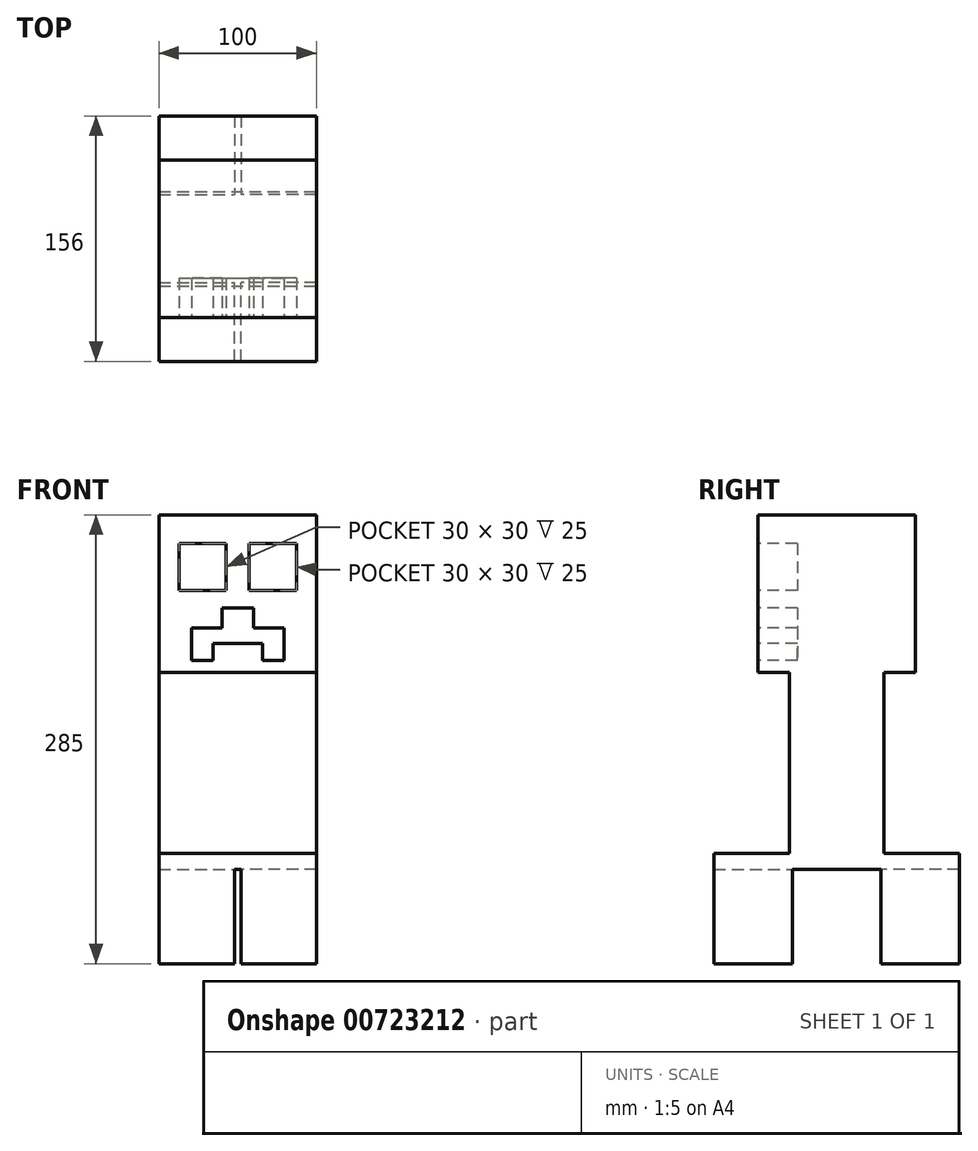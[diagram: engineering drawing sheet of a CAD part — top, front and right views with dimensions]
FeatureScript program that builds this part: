
annotation { "Feature Type Name" : "Feature", "Feature Type Description" : "" }
export const myFeature = defineFeature(function(context is Context, id is Id, definition is map)
    precondition{}
    {
        {
            var Q0;
            Q0=qCreatedBy(makeId("Top.planeOp"),FACE);
            var sketch = newSketch(context, id + "F0", { "sketchPlane" : qUnion([Q0])});
            skLineSegment(sketch, "E0.bottom", {"start": v(50, -50) * mm, "end": v(-50, -50) * mm});
            skLineSegment(sketch, "E0.top", {"start": v(50, 50) * mm, "end": v(-50, 50) * mm});
            skLineSegment(sketch, "E0.left", {"start": v(50, -50) * mm, "end": v(50, 50) * mm});
            skLineSegment(sketch, "E0.right", {"start": v(-50, -50) * mm, "end": v(-50, 50) * mm});
            skPoint(sketch, "E0.middle", {"position": v(0, 0) * mm});
            skSolve(sketch);
        }
        {
            var Q0;
            Q0 = qSketchRegion(id + "F0", true);
            extrude(context, id + "F1", {"entities" : qUnion([Q0]), "depth" : 100 * mm, "offsetDistance" : 25 * mm});
        }
        {
            var Q0;
            Q0=makeQuery(id+"F1.opExtrude","SWEPT_FACE",FACE,{"disambiguationData":[OSD([sQuery(id+"F0.wireOp",EDGE,"E0.bottom")])]});
            var sketch = newSketch(context, id + "F2", { "sketchPlane" : qUnion([Q0])});
            skLineSegment(sketch, "E1.bottom", {"start": v(-37.3, 82.01) * mm, "end": v(-7.3, 82.01) * mm});
            skLineSegment(sketch, "E1.top", {"start": v(-37.3, 52.01) * mm, "end": v(-7.3, 52.01) * mm});
            skLineSegment(sketch, "E1.left", {"start": v(-37.3, 82.01) * mm, "end": v(-37.3, 52.01) * mm});
            skLineSegment(sketch, "E1.right", {"start": v(-7.3, 82.01) * mm, "end": v(-7.3, 52.01) * mm});
            skLineSegment(sketch, "E2.MirrorCS", {"start": v(7.3, 82.01) * mm, "end": v(7.3, 52.01) * mm});
            skLineSegment(sketch, "E3.MirrorCS", {"start": v(37.3, 82.01) * mm, "end": v(37.3, 52.01) * mm});
            skLineSegment(sketch, "E4.MirrorCS", {"start": v(37.3, 82.01) * mm, "end": v(7.3, 82.01) * mm});
            skLineSegment(sketch, "E5.MirrorCS", {"start": v(37.3, 52.01) * mm, "end": v(7.3, 52.01) * mm});
            skLineSegment(sketch, "E6", {"start": v(0, 40.98) * mm, "end": v(-9.95, 40.98) * mm});
            skLineSegment(sketch, "E7", {"start": v(-9.95, 40.98) * mm, "end": v(-9.95, 28.34) * mm});
            skLineSegment(sketch, "E8", {"start": v(-9.95, 28.34) * mm, "end": v(-29.4, 28.34) * mm});
            skLineSegment(sketch, "E9", {"start": v(-29.4, 28.34) * mm, "end": v(-29.4, 7.56) * mm});
            skLineSegment(sketch, "E10", {"start": v(-29.4, 7.56) * mm, "end": v(-15.66, 7.56) * mm});
            skLineSegment(sketch, "E11", {"start": v(-15.66, 7.56) * mm, "end": v(-15.66, 18.36) * mm});
            skLineSegment(sketch, "E12", {"start": v(-15.66, 18.36) * mm, "end": v(0, 18.36) * mm});
            skLineSegment(sketch, "E13.MirrorCS", {"start": v(9.95, 40.98) * mm, "end": v(9.95, 28.34) * mm});
            skLineSegment(sketch, "E14.MirrorCS", {"start": v(0, 40.98) * mm, "end": v(9.95, 40.98) * mm});
            skLineSegment(sketch, "E15.MirrorCS", {"start": v(9.95, 28.34) * mm, "end": v(29.4, 28.34) * mm});
            skLineSegment(sketch, "E16.MirrorCS", {"start": v(29.4, 28.34) * mm, "end": v(29.4, 7.56) * mm});
            skLineSegment(sketch, "E17.MirrorCS", {"start": v(29.4, 7.56) * mm, "end": v(15.66, 7.56) * mm});
            skLineSegment(sketch, "E18.MirrorCS", {"start": v(15.66, 18.36) * mm, "end": v(0, 18.36) * mm});
            skLineSegment(sketch, "E19.MirrorCS", {"start": v(15.66, 7.56) * mm, "end": v(15.66, 18.36) * mm});
            skSolve(sketch);
        }
        {
            var Q0;
            Q0 = qSketchRegion(id + "F2", true);
            extrude(context, id + "F3", {"entities" : qUnion([Q0]), "operationType" : NewBodyOperationType.REMOVE, "oppositeDirection" : true, "depth" : 25 * mm, "offsetDistance" : 25 * mm});
        }
        {
            var Q0;
            Q0=makeQuery(id+"F1.opExtrude","CAP_FACE",FACE,{"disambiguationData":[OSD([sQuery(id+"F0.wireOp",EDGE,"E0.bottom"),sQuery(id+"F0.wireOp",EDGE,"E0.top"),sQuery(id+"F0.wireOp",EDGE,"E0.left"),sQuery(id+"F0.wireOp",EDGE,"E0.right")])],"isStart":true});
            var sketch = newSketch(context, id + "F4", { "sketchPlane" : qUnion([Q0])});
            skLineSegment(sketch, "E20", {"start": v(50, 0) * mm, "end": v(-50, 0) * mm});
            skLineSegment(sketch, "E21", {"start": v(0, -50) * mm, "end": v(0, 50) * mm});
            skLineSegment(sketch, "E22.bottom", {"start": v(-50, -30) * mm, "end": v(50, -30) * mm});
            skLineSegment(sketch, "E22.top", {"start": v(-50, 30) * mm, "end": v(50, 30) * mm});
            skLineSegment(sketch, "E22.left", {"start": v(-50, -30) * mm, "end": v(-50, 30) * mm});
            skLineSegment(sketch, "E22.right", {"start": v(50, -30) * mm, "end": v(50, 30) * mm});
            skPoint(sketch, "E22.middle", {"position": v(0, 0) * mm});
            skSolve(sketch);
        }
        {
            var Q0;
            Q0 = qSketchRegion(id + "F4", true);
            extrude(context, id + "F5", {"entities" : qUnion([Q0]), "operationType" : NewBodyOperationType.ADD, "depth" : 115 * mm, "offsetDistance" : 25 * mm});
        }
        {
            var Q0;
            Q0=makeQuery(id+"F5.opExtrude","CAP_FACE",FACE,{"disambiguationData":[OSD([sQuery(id+"F4.wireOp",EDGE,"E22.bottom"),sQuery(id+"F4.wireOp",EDGE,"E22.top"),sQuery(id+"F4.wireOp",EDGE,"E22.left"),sQuery(id+"F4.wireOp",EDGE,"E22.right")])],"isStart":false});
            var sketch = newSketch(context, id + "F6", { "sketchPlane" : qUnion([Q0])});
            skLineSegment(sketch, "E23.bottom", {"start": v(50, -78) * mm, "end": v(-50, -78) * mm});
            skLineSegment(sketch, "E23.top", {"start": v(50, 78) * mm, "end": v(-50, 78) * mm});
            skLineSegment(sketch, "E23.left", {"start": v(50, -78) * mm, "end": v(50, 78) * mm});
            skLineSegment(sketch, "E23.right", {"start": v(-50, -78) * mm, "end": v(-50, 78) * mm});
            skPoint(sketch, "E23.middle", {"position": v(0, 0) * mm});
            skSolve(sketch);
        }
        {
            var Q0;
            Q0 = qSketchRegion(id + "F6", true);
            extrude(context, id + "F7", {"entities" : qUnion([Q0]), "operationType" : NewBodyOperationType.ADD, "depth" : 10 * mm, "offsetDistance" : 25 * mm});
        }
        {
            var Q0;
            Q0=makeQuery(id+"F7.opExtrude","CAP_FACE",FACE,{"disambiguationData":[OSD([sQuery(id+"F6.wireOp",EDGE,"E23.bottom"),sQuery(id+"F6.wireOp",EDGE,"E23.top"),sQuery(id+"F6.wireOp",EDGE,"E23.left"),sQuery(id+"F6.wireOp",EDGE,"E23.right")])],"isStart":false});
            var sketch = newSketch(context, id + "F8", { "sketchPlane" : qUnion([Q0])});
            skLineSegment(sketch, "E24.bottom", {"start": v(-50, 78) * mm, "end": v(-2, 78) * mm});
            skLineSegment(sketch, "E24.top", {"start": v(-50, 28) * mm, "end": v(-2, 28) * mm});
            skLineSegment(sketch, "E24.left", {"start": v(-50, 78) * mm, "end": v(-50, 28) * mm});
            skLineSegment(sketch, "E24.right", {"start": v(-2, 78) * mm, "end": v(-2, 28) * mm});
            skLineSegment(sketch, "E25.bottom", {"start": v(50, 78) * mm, "end": v(2, 78) * mm});
            skLineSegment(sketch, "E25.top", {"start": v(50, 28) * mm, "end": v(2, 28) * mm});
            skLineSegment(sketch, "E25.left", {"start": v(50, 78) * mm, "end": v(50, 28) * mm});
            skLineSegment(sketch, "E25.right", {"start": v(2, 78) * mm, "end": v(2, 28) * mm});
            skLineSegment(sketch, "E26.bottom", {"start": v(-50, -78) * mm, "end": v(-2, -78) * mm});
            skLineSegment(sketch, "E26.top", {"start": v(-50, -28) * mm, "end": v(-2, -28) * mm});
            skLineSegment(sketch, "E26.left", {"start": v(-50, -78) * mm, "end": v(-50, -28) * mm});
            skLineSegment(sketch, "E26.right", {"start": v(-2, -78) * mm, "end": v(-2, -28) * mm});
            skLineSegment(sketch, "E27.bottom", {"start": v(50, -78) * mm, "end": v(2, -78) * mm});
            skLineSegment(sketch, "E27.top", {"start": v(50, -28) * mm, "end": v(2, -28) * mm});
            skLineSegment(sketch, "E27.left", {"start": v(50, -78) * mm, "end": v(50, -28) * mm});
            skLineSegment(sketch, "E27.right", {"start": v(2, -78) * mm, "end": v(2, -28) * mm});
            skSolve(sketch);
        }
        {
            var Q0;
            Q0 = qSketchRegion(id + "F8", true);
            extrude(context, id + "F9", {"entities" : qUnion([Q0]), "operationType" : NewBodyOperationType.ADD, "depth" : 60 * mm, "offsetDistance" : 25 * mm});
        }
    });
